# Revit family: Sanitary_Taps-Mixers_hansgrohe_72551XXX-Rebris-E-Single-lever-basin-mixer-110-CoolStart-with-metal-pop-up-waste-set
name_source: partatom
category: Plumbing Fixtures
revit_build: Autodesk Revit 2018 (Build: 20190510_1515(x64)
units: mm (PartAtom-declared; Revit-internal decimal feet)

## family parameters
Always vertical = No
Cut with Voids When Loaded = No
OmniClass Number = 23.31.11.00
OmniClass Title = Faucets
Part Type = Normal
Room Calculation Point = No
Round Connector Dimension = Use Diameter
Shared = No
Work Plane-Based = Yes

## types (2) — shared parameters
Always visible = Yes
BIMobject category = Taps & Mixers
Cold Water Inlet = 9.525 mm  [stored 0.03125 ft]
Cold Water Inlet Description = Cold Water Inlet 9.525mm
Default Elevation = 1219.2 mm  [stored 4 ft]
Description = Rebris E Single lever basin mixer 110 CoolStart with metal pop-up waste set
Edition number = 1
Hot Water Inlet = 9.525 mm  [stored 0.03125 ft]
Hot Water Inlet Description = Hot Water Inlet 9.525mm
IFC Classification = Valve
Manufacturer = Hansgrohe
Manufacturer name = hansgrohe
Model = 72551XXX Rebris E Single lever basin mixer 110 CoolStart with metal pop-up waste set
OmniClass Code = 23-31 11 00
OmniClass Description = Faucets
Product Guid = 510fcd82-7726-4bca-bd9e-e11d9962dde1
Product SKU = 72551XXX
Product data url = https://bimobject.com
Product family = Rebris E
Product group = Basin mixers
Product name = 72551XXX Rebris E Single lever basin mixer 110 CoolStart with metal pop-up waste set
Product url = https://www.hansgrohe.com
QR code = https://bimobject.com
URL = https://www.hansgrohe.com

## per-type parameters (varying)
| type | Main material |
| 670 Matt Black | Hansgrohe - Metal - 670 Matt Black |
| 000 Chrome | Hansgrohe - Metal - 000 Chrome |

note: [stored X ft] marks values corroborated as IEEE doubles in the binary element streams (Revit-internal decimal feet)

## geometry (parser evidence)
native form markers: Sweep x6
no freeform markers — native parametric forms only
